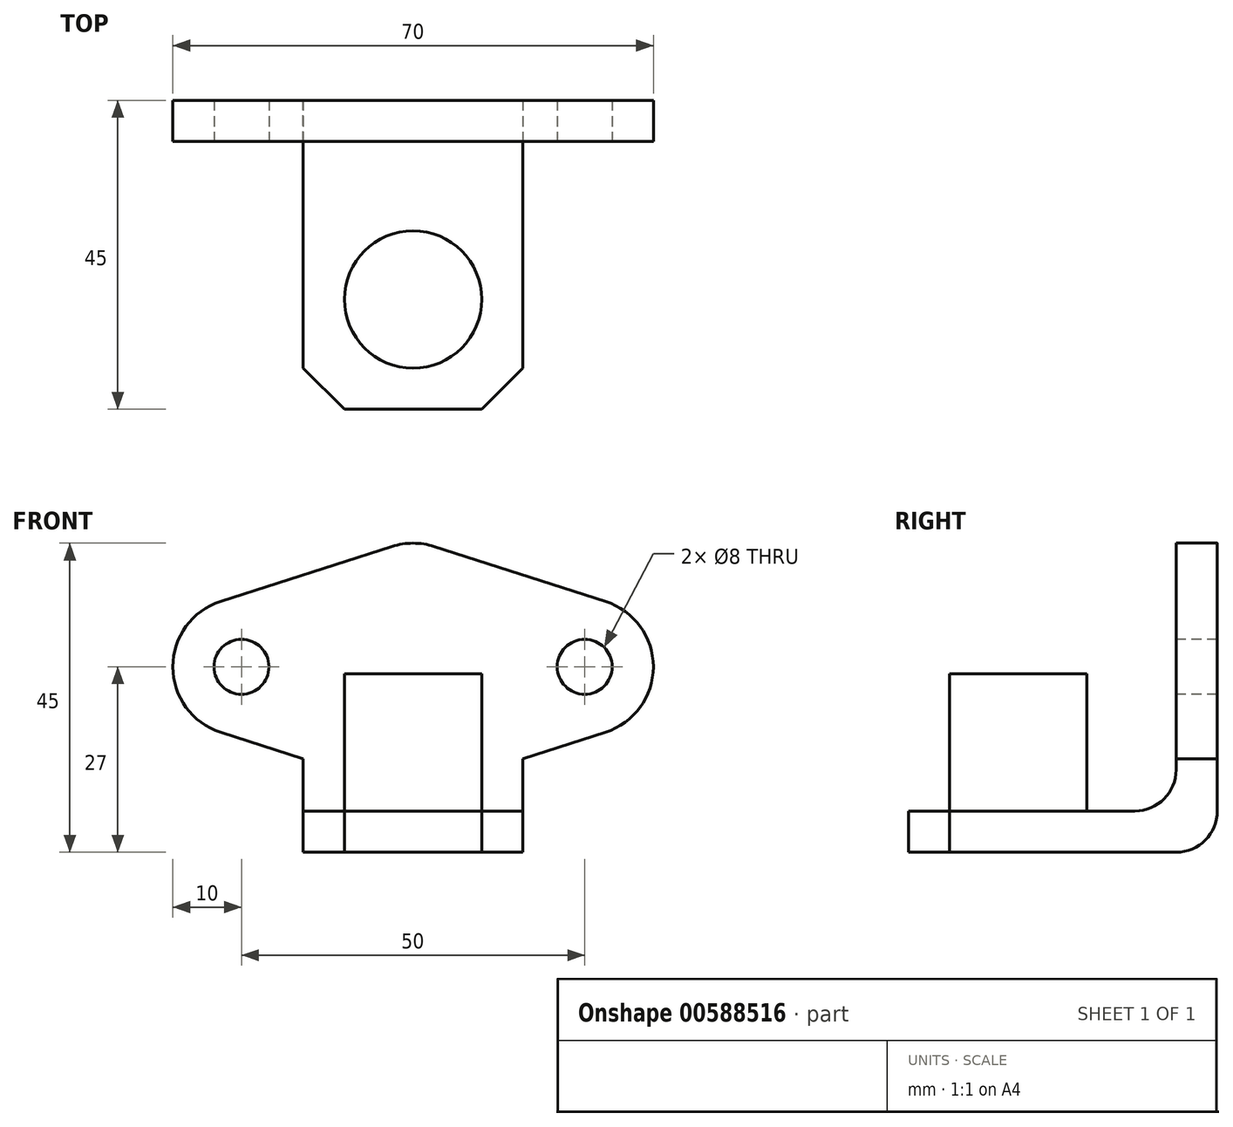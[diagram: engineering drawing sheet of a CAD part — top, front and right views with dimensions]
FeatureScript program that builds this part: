
annotation { "Feature Type Name" : "Feature", "Feature Type Description" : "" }
export const myFeature = defineFeature(function(context is Context, id is Id, definition is map)
    precondition{}
    {
        {
            var Q0;
            Q0=qCreatedBy(makeId("Right.planeOp"),FACE);
            var sketch = newSketch(context, id + "F0", { "sketchPlane" : qUnion([Q0])});
            skLineSegment(sketch, "E0", {"start": v(0, 0) * mm, "end": v(0, 6) * mm});
            skLineSegment(sketch, "E1", {"start": v(0, 6) * mm, "end": v(33, 6) * mm});
            skLineSegment(sketch, "E2", {"start": v(39, 12) * mm, "end": v(39, 45) * mm});
            skLineSegment(sketch, "E3", {"start": v(39, 45) * mm, "end": v(45, 45) * mm});
            skLineSegment(sketch, "E4", {"start": v(45, 45) * mm, "end": v(45, 6) * mm});
            skLineSegment(sketch, "E5", {"start": v(39, 0) * mm, "end": v(0, 0) * mm});
            skPoint(sketch, "E6.visualSharp", {"position": v(39, 6) * mm});
            skArc(sketch, "E6.filletArc", {"start": v(33, 6) * mm, "mid": v(37.24, 7.76) * mm, "end": v(39, 12) * mm});
            skPoint(sketch, "E7.visualSharp", {"position": v(45, 0) * mm});
            skArc(sketch, "E7.filletArc", {"start": v(39, 0) * mm, "mid": v(43.24, 1.76) * mm, "end": v(45, 6) * mm});
            skSolve(sketch);
        }
        {
            var Q0;
            Q0 = qSketchRegion(id + "F0", true);
            extrude(context, id + "F1", {"entities" : qUnion([Q0]), "depth" : 70 * mm, "offsetDistance" : 25 * mm});
        }
        {
            var Q0;
            Q0=qCreatedBy(makeId("Front.planeOp"),FACE);
            var sketch = newSketch(context, id + "F2", { "sketchPlane" : qUnion([Q0])});
            skLineSegment(sketch, "E8", {"start": v(19, 0) * mm, "end": v(19, 13.62) * mm});
            skLineSegment(sketch, "E9", {"start": v(51, 13.62) * mm, "end": v(51, 0) * mm});
            skLineSegment(sketch, "E10", {"start": v(51, 0) * mm, "end": v(19, 0) * mm});
            skCircle(sketch, "E11", {"center": v(10, 27) * mm, "radius": 4 * mm});
            skArc(sketch, "E12", {"start": v(6.95, 36.52) * mm, "mid": v(0, 27) * mm, "end": v(6.95, 17.48) * mm});
            skCircle(sketch, "E13", {"center": v(60, 27) * mm, "radius": 4 * mm});
            skArc(sketch, "E14", {"start": v(63.05, 17.48) * mm, "mid": v(70, 27) * mm, "end": v(63.05, 36.52) * mm});
            skArc(sketch, "E15", {"start": v(38.05, 44.52) * mm, "mid": v(35, 45) * mm, "end": v(31.95, 44.52) * mm});
            skLineSegment(sketch, "E16", {"start": v(31.95, 44.52) * mm, "end": v(6.95, 36.52) * mm});
            skLineSegment(sketch, "E17", {"start": v(38.05, 44.52) * mm, "end": v(63.05, 36.52) * mm});
            skLineSegment(sketch, "E18", {"start": v(6.95, 17.48) * mm, "end": v(19, 13.62) * mm});
            skLineSegment(sketch, "E19", {"start": v(63.05, 17.48) * mm, "end": v(51, 13.62) * mm});
            skLineSegment(sketch, "E20", {"start": v(10, 27) * mm, "end": v(60, 27) * mm, "construction": true});
            skLineSegment(sketch, "E21", {"start": v(35, 45) * mm, "end": v(70, 45) * mm});
            skPoint(sketch, "E21.endSnap0", {"position": v(70, 27) * mm});
            skLineSegment(sketch, "E22", {"start": v(70, 45) * mm, "end": v(70, 0) * mm});
            skLineSegment(sketch, "E23", {"start": v(70, 0) * mm, "end": v(0, 0) * mm});
            skLineSegment(sketch, "E24", {"start": v(0, 0) * mm, "end": v(0, 45) * mm});
            skLineSegment(sketch, "E25", {"start": v(0, 45) * mm, "end": v(35, 45) * mm});
            skSolve(sketch);
        }
        {
            var Q0;
            Q0=makeQuery(id+"F2.imprint","IMPRINT",FACE,{"disambiguationData":[TD([[makeQuery(id+"F2.imprint","IMPRINT",EDGE,{"derivedFrom":sQuery(id+"F2.wireOp",EDGE,"E11")}),1.0]])]});
            var Q1;
            Q1=makeQuery(id+"F2.imprint","IMPRINT",FACE,{"disambiguationData":[TD([[makeQuery(id+"F2.imprint","IMPRINT",EDGE,{"derivedFrom":sQuery(id+"F2.wireOp",EDGE,"E13")}),1.0]])]});
            var Q2;
            {var subQ1=sQuery(id+"F2.wireOp",EDGE,"E17");Q2=makeQuery(id+"F2.imprint","IMPRINT",FACE,{"disambiguationData":[TD([[makeQuery(id+"F2.imprint","IMPRINT",EDGE,{"derivedFrom":subQ1}),1.0]])]});}
            var Q3;
            {var subQ6=sQuery(id+"F2.wireOp",EDGE,"E9");Q3=makeQuery(id+"F2.imprint","IMPRINT",FACE,{"disambiguationData":[TD([[makeQuery(id+"F2.imprint","IMPRINT",EDGE,{"derivedFrom":subQ6}),1.0]])]});}
            var Q4;
            {var subQ2=sQuery(id+"F2.wireOp",EDGE,"E8");Q4=makeQuery(id+"F2.imprint","IMPRINT",FACE,{"disambiguationData":[TD([[makeQuery(id+"F2.imprint","IMPRINT",EDGE,{"derivedFrom":subQ2}),1.0]])]});}
            var Q5;
            {var subQ4=sQuery(id+"F2.wireOp",EDGE,"E16");Q5=makeQuery(id+"F2.imprint","IMPRINT",FACE,{"disambiguationData":[TD([[makeQuery(id+"F2.imprint","IMPRINT",EDGE,{"derivedFrom":subQ4}),-1.0]])]});}
            extrude(context, id + "F3", {"entities" : qUnion([Q0, Q1, Q2, Q3, Q4, Q5]), "operationType" : NewBodyOperationType.REMOVE, "endBound" : BoundingType.THROUGH_ALL, "oppositeDirection" : true, "depth" : 25 * mm, "offsetDistance" : 25 * mm});
        }
        {
            var Q0;
            Q0=qCreatedBy(makeId("Top.planeOp"),FACE);
            var sketch = newSketch(context, id + "F4", { "sketchPlane" : qUnion([Q0])});
            skLineSegment(sketch, "E26", {"start": v(25, 0) * mm, "end": v(19, 6) * mm});
            skLineSegment(sketch, "E27", {"start": v(19, 6) * mm, "end": v(19, 0) * mm});
            skLineSegment(sketch, "E28", {"start": v(19, 0) * mm, "end": v(25, 0) * mm});
            skLineSegment(sketch, "E29", {"start": v(51, 0) * mm, "end": v(45, 0) * mm});
            skLineSegment(sketch, "E30", {"start": v(45, 0) * mm, "end": v(51, 6) * mm});
            skLineSegment(sketch, "E31", {"start": v(51, 6) * mm, "end": v(51, 0) * mm});
            skCircle(sketch, "E32", {"center": v(35, 16) * mm, "radius": 8 * mm});
            skSolve(sketch);
        }
        {
            var Q0;
            Q0=makeQuery(id+"F4.imprint","IMPRINT",FACE,{"disambiguationData":[TD([[makeQuery(id+"F4.imprint","IMPRINT",EDGE,{"derivedFrom":sQuery(id+"F4.wireOp",EDGE,"E32")}),1.0]])]});
            var Q1;
            Q1=makeQuery(id+"F4.imprint","IMPRINT",FACE,{"disambiguationData":[TD([[makeQuery(id+"F4.imprint","IMPRINT",EDGE,{"derivedFrom":sQuery(id+"F4.wireOp",EDGE,"E26")}),1.0]])]});
            var Q2;
            Q2=makeQuery(id+"F4.imprint","IMPRINT",FACE,{"disambiguationData":[TD([[makeQuery(id+"F4.imprint","IMPRINT",EDGE,{"derivedFrom":sQuery(id+"F4.wireOp",EDGE,"E29")}),-1.0]])]});
            extrude(context, id + "F5", {"entities" : qUnion([Q0, Q1, Q2]), "operationType" : NewBodyOperationType.REMOVE, "endBound" : BoundingType.THROUGH_ALL, "depth" : 25 * mm, "offsetDistance" : 25 * mm});
        }
        {
            var Q0;
            Q0=makeQuery(id+"F1.opExtrude","SWEPT_FACE",FACE,{"disambiguationData":[OSD([sQuery(id+"F0.wireOp",EDGE,"E0")])]});
            cPlane(context, id + "F6", {"entities" : qUnion([Q0]), "cplaneType" : CPlaneType.OFFSET, "offset" : 16 * mm, "oppositeDirection" : true, "width" : 150 * mm, "height" : 150 * mm});
        }
        {
            var Q0;
            Q0=qCreatedBy(id+"F6.planeOp",FACE);
            var sketch = newSketch(context, id + "F7", { "sketchPlane" : qUnion([Q0])});
            skLineSegment(sketch, "E33", {"start": v(35, 0) * mm, "end": v(35, 26) * mm});
            skLineSegment(sketch, "E34", {"start": v(35, 26) * mm, "end": v(45, 26) * mm});
            skLineSegment(sketch, "E35", {"start": v(45, 26) * mm, "end": v(45, 6) * mm});
            skLineSegment(sketch, "E36", {"start": v(45, 6) * mm, "end": v(43, 6) * mm});
            skLineSegment(sketch, "E37", {"start": v(43, 6) * mm, "end": v(43, 0) * mm});
            skLineSegment(sketch, "E38", {"start": v(43, 0) * mm, "end": v(35, 0) * mm});
            skSolve(sketch);
        }
        {
            var Q0;
            Q0=makeQuery(id+"F7.imprint","IMPRINT",FACE,{"disambiguationData":[TD([[makeQuery(id+"F7.imprint","IMPRINT",EDGE,{"derivedFrom":sQuery(id+"F7.wireOp",EDGE,"E33")}),-1.0]])]});
            var Q1;
            Q1=sQuery(id+"F7.wireOp",EDGE,"E33");
            revolve(context, id + "F8", {"operationType" : NewBodyOperationType.ADD, "entities" : qUnion([Q0]), "axis" : qUnion([Q1]), "revolveType" : RevolveType.FULL});
        }
    });
